# Revit family: CVRL-CM
name_source: partatom
category: Lighting Fixtures
revit_build: Autodesk Revit 2013 (Build: 20130531_2115(x64)
units: mm (PartAtom-declared; Revit-internal decimal feet)

## types (5) — shared parameters
Assembly Code = D5020200
Color Filter = 16777215
Default Elevation = 48"
Description = A smooth curvature shape with a glowing center optics that span the radius of the luminaire housing is delivered with the Curv Radial Lens.
Dimming Lamp Color Temperature Shift = <None>
Emit Shape Visible in Rendering = No
Emit from Rectangle Length = 46"
Emit from Rectangle Width = 7"
Glass = Hubbell - White Glass
Housing Material = Hubbell - White
Lamp = T5, T5HO, T8
Load Classification = Lighting
Manufacturer = Alera Lighting
Model = CVRL
Photometric Notes = More IES files download on Photometric Web Link
Photometric Web Link = https://www.hubbell.com
Power Factor = 1
Product Documentation Link = https://hubbellcdn.com
Product Page URL = https://www.hubbell.com
Row Length = 48"
Suspension Height = 48"
Tilt Angle = -90.00°
URL = https://www.hubbell.com
Voltage = 120 V

## per-type parameters (varying)
| type | Apparent Load | Lamp Type | Photometric Web File | Watts |
| CVRL-4-2T8-OA-EPU | 29 VA | Two T8 Lamps | CVRL-4-2T8-OA-EPU.ies | 29 W |
| CVRL-4-2T5-OA-EPU | 62 VA | Two T5 Lamps | CVRL-4-2T5-OA-EPU.ies | 62 W |
| CVRL-3T8-EPU | 84 VA | Three T8 Lamps | CVRL-3T8-EPU.ies | 84 W |
| CVRL-3T8-0/100-EPU | 79 VA | Three T8 Lamps | CVRL-3T8-0 100-EPU 3 lamp with 100 downlight cover.ies | 79 W |
| CVRL-1T8-EPU | 29 VA | One T8 Lamp | CVRL-1T8-EPU.ies | 29 W |

## geometry (parser evidence)
native form markers: Blend x4, Sweep x4
no freeform markers — native parametric forms only
